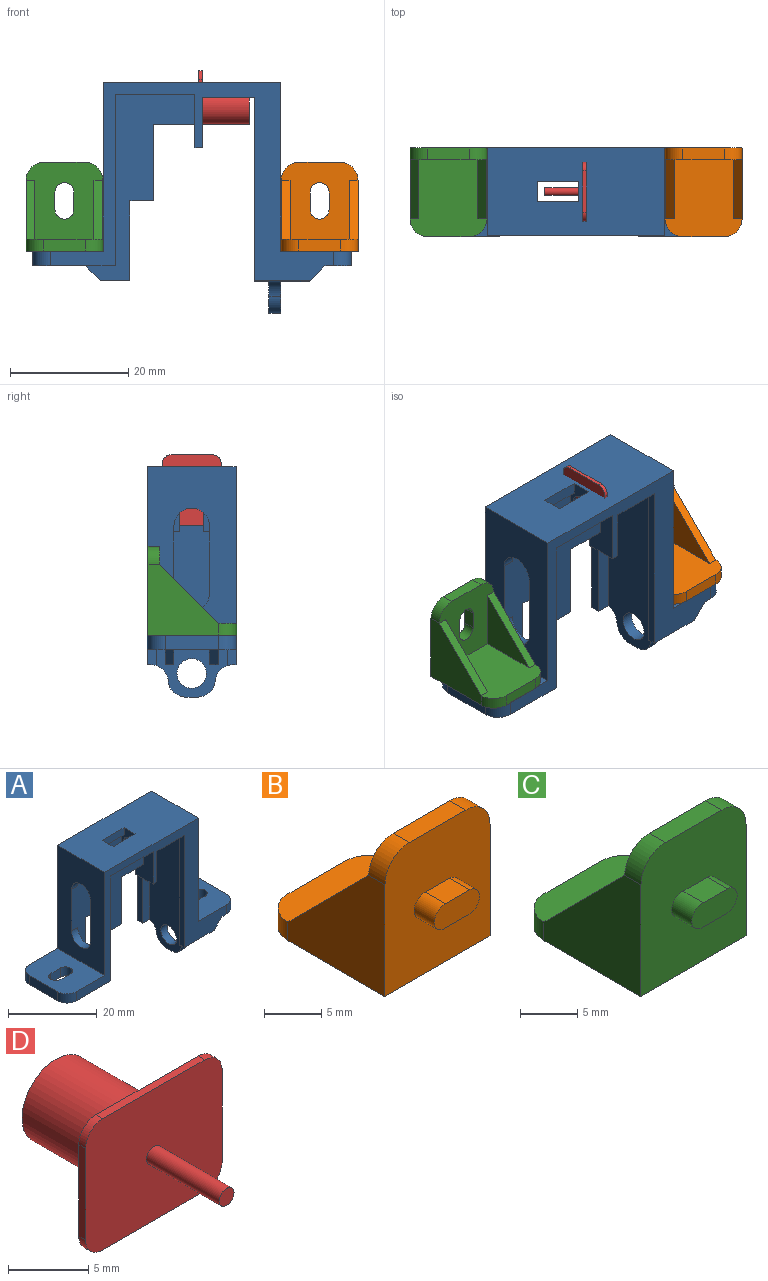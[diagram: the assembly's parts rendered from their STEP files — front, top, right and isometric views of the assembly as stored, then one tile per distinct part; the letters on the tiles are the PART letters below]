
ASSEMBLY  parts=4 mates=3
PART A: 82 faces, bbox 54x15x39 mm
  f0: plane 31.5x18.5mm, normal (0,1,0), area 195.1mm2, adj f3,f13,f16,f20,f22,f38,f54,f73
  f1: plane 31.5x18.5mm, normal (0,-1,0), area 195.1mm2, adj f2,f12,f16,f19,f22,f39,f54,f74
  f2: plane 5x1.5mm, normal (0,0,-1), area 7.5mm2, adj f1,f36,f74,f78
  f3: plane 5x1.5mm, normal (0,0,-1), area 7.5mm2, adj f0,f37,f73,f75
  f4: plane 15x12mm, normal (0,0,-1), area 136mm2, adj f7,f21,f25,f32,f33,f34,f35,f45
  f5: plane 11.25x4.9mm, normal (0,0,-1), area 51.4mm2, adj f6,f7,f43,f57,f61,f62
  f6: plane 38x12mm, normal (-1,0,0), area 401.7mm2, adj f5,f57,f58,f60,f61,f68,f69,f70
  f7: plane 48x33.5mm, normal (0,1,0), area 336mm2, adj f4,f5,f10,f13,f16,f18,f22,f23
  f8: plane 3x3mm, normal (1,0,0), area 1.9mm2, adj f36,f54,f56
  f9: plane 3x3mm, normal (1,0,0), area 1.9mm2, adj f37,f54,f56
  f10: plane 28.5x15mm, normal (-1,0,0), area 330.2mm2, adj f7,f18,f21,f24,f36,f37,f55,f56
  f11: plane 7x0.75mm, normal (0,0,-1), area 5.3mm2, adj f16,f40,f41,f53
  f12: plane 13.5x3mm, normal (0,0,-1), area 40.5mm2, adj f1,f16,f21,f39
  f13: plane 13.5x3mm, normal (0,0,-1), area 40.5mm2, adj f0,f7,f16,f38
  f14: plane 9.5x6mm, normal (1,0,0), area 42.9mm2, adj f22,f36,f37,f55
  f15: plane 5.5x1.25mm, normal (0,0,-1), area 6.9mm2, adj f16,f21,f43,f51
  f16: plane 15x11mm, normal (-1,0,0), area 87.7mm2, adj f0,f1,f7,f11,f12,f13,f15,f17
  f17: plane 7x0.75mm, normal (0,0,-1), area 5.2mm2, adj f16,f41,f42,f52
  f18: plane 30x15mm, normal (0,0,1), area 425.5mm2, adj f7,f10,f16,f21,f26,f40,f41,f42
  f19: plane 13x1.5mm, normal (1,0,0), area 19.5mm2, adj f1,f36,f54,f77
  f20: plane 13x1.5mm, normal (1,0,0), area 19.5mm2, adj f0,f37,f54,f76
  f21: plane 48x33.5mm, normal (0,-1,0), area 336mm2, adj f4,f10,f12,f15,f16,f18,f22,f23
  f22: plane 15x14mm, normal (0,0,-1), area 173.5mm2, adj f0,f1,f7,f14,f21,f27,f28,f29
  f23: plane 15x12mm, normal (0,0,1), area 158.5mm2, adj f7,f21,f25,f26,f32,f33,f34,f35
  f24: plane 15x12mm, normal (0,0,1), area 158.5mm2, adj f7,f10,f21,f27,f28,f29,f30,f31
  f25: plane 9x2.5mm, normal (1,0,0), area 22.5mm2, adj f4,f23,f45,f47
  f26: plane 28.5x15mm, normal (1,0,0), area 427.5mm2, adj f7,f18,f21,f23
  f27: plane 9x2.5mm, normal (-1,0,0), area 22.5mm2, adj f22,f24,f46,f48
  f28: plane 3x2.5mm, normal (0,1,0), area 7.5mm2, adj f22,f24,f29,f31
  f29: cylinder r=1.6mm len=3.2mm, axis (0,0,-1), area 12.6mm2, adj f22,f24,f28,f30
  f30: plane 3x2.5mm, normal (0,-1,0), area 7.5mm2, adj f22,f24,f29,f31
  f31: cylinder r=1.6mm len=3.2mm, axis (0,0,-1), area 12.6mm2, adj f22,f24,f28,f30
  f32: cylinder r=1.6mm len=3.2mm, axis (0,0,-1), area 12.6mm2, adj f4,f23,f33,f35
  f33: plane 3x2.5mm, normal (0,-1,0), area 7.5mm2, adj f4,f23,f32,f34
  f34: cylinder r=1.6mm len=3.2mm, axis (0,0,-1), area 12.6mm2, adj f4,f23,f33,f35
  f35: plane 3x2.5mm, normal (0,1,0), area 7.5mm2, adj f4,f23,f32,f34
  f36: plane 26.5x11.5mm, normal (0,1,0), area 150.6mm2, adj f2,f8,f10,f14,f19,f22,f54,f55
  f37: plane 26.5x11.5mm, normal (0,-1,0), area 150.6mm2, adj f3,f9,f10,f14,f20,f22,f54,f55
  f38: plane 29x3mm, normal (1,0,0), area 87mm2, adj f0,f7,f13,f22
  f39: plane 29x3mm, normal (1,0,0), area 87mm2, adj f1,f12,f21,f22
  f40: plane 7x2mm, normal (0,1,0), area 14mm2, adj f11,f16,f18,f41
  f41: plane 7x5mm, normal (1,0,0), area 32mm2, adj f11,f17,f18,f40,f42,f52,f53,f54
  f42: plane 7x2mm, normal (0,-1,0), area 14mm2, adj f16,f17,f18,f41
  f43: plane 15x10mm, normal (1,0,0), area 98.7mm2, adj f5,f7,f15,f21,f44,f49,f50,f51
  f44: plane 5.5x1.25mm, normal (0,0,-1), area 6.9mm2, adj f7,f16,f43,f49
  f45: cylinder r=3mm len=3mm, axis (0,0,1), area 11.8mm2, adj f4,f7,f23,f25
  f46: cylinder r=3mm len=3mm, axis (0,0,-1), area 11.8mm2, adj f7,f22,f24,f27
  f47: cylinder r=3mm len=3mm, axis (0,0,-1), area 11.8mm2, adj f4,f21,f23,f25
  f48: cylinder r=3mm len=3mm, axis (0,0,1), area 11.8mm2, adj f21,f22,f24,f27
  f49: plane 7x1.25mm, normal (0,-1,0), area 8.8mm2, adj f16,f43,f44,f50
  f50: cylinder r=2mm len=4mm, axis (1,0,0), area 7.9mm2, adj f16,f43,f49,f51
  f51: plane 7x1.25mm, normal (0,1,0), area 8.8mm2, adj f15,f16,f43,f50
  f52: plane 7x5mm, normal (0,-1,0), area 35mm2, adj f16,f17,f41,f54
  f53: plane 7x5mm, normal (0,1,0), area 35mm2, adj f11,f16,f41,f54
  f54: plane 13.5x9mm, normal (0,0,-1), area 67mm2, adj f0,f1,f8,f9,f16,f19,f20,f36
  f55: cylinder r=3mm len=6mm, axis (-1,0,0), area 18.8mm2, adj f10,f14,f36,f37
  f56: cylinder r=3mm len=6mm, axis (-1,0,0), area 18.8mm2, adj f8,f9,f10,f36,f37
  f57: cylinder r=3mm len=11.25mm, axis (1,0,0), area 70.7mm2, adj f5,f6,f43,f58
  f58: plane 11.25x4.9mm, normal (0,0,-1), area 51.4mm2, adj f6,f21,f43,f57,f59,f60
  f59: plane 31.16x1.5mm, normal (-1,0,0), area 46.6mm2, adj f21,f58,f60,f65,f80
  f60: plane 31.16x2.5mm, normal (0,1,0), area 77.9mm2, adj f6,f58,f59,f80
  f61: plane 31.16x2.5mm, normal (0,-1,0), area 77.9mm2, adj f5,f6,f62,f81
  f62: plane 31.16x1.5mm, normal (-1,0,0), area 46.6mm2, adj f5,f7,f61,f67,f81
  f63: plane 12x8mm, normal (1,0,0), area 54.1mm2, adj f4,f64,f66,f68,f69,f70,f79,f80
  f64: plane 7.5x2.66mm, normal (0,1,0), area 16.4mm2, adj f4,f63,f71,f80
  f65: plane 9.5x0.52mm, normal (0,0,-1), area 4.9mm2, adj f21,f59,f71,f80
  f66: plane 7.5x2.66mm, normal (0,-1,0), area 16.4mm2, adj f4,f63,f72,f81
  f67: plane 9.5x0.52mm, normal (0,0,-1), area 4.9mm2, adj f7,f62,f72,f81
  f68: plane 2x2mm, normal (0,0,-1), area 4mm2, adj f6,f63,f69,f70
  f69: cylinder r=3mm len=2.99mm, axis (-1,0,0), area 8.9mm2, adj f6,f63,f68,f81
  f70: cylinder r=3mm len=2.99mm, axis (1,0,0), area 8.9mm2, adj f6,f63,f68,f80
  f71: plane 2.66x2.66mm, normal (0.71,0,-0.71), area 5.4mm2, adj f4,f21,f64,f65,f80
  f72: plane 2.66x2.66mm, normal (0.71,0,-0.71), area 5.4mm2, adj f4,f7,f66,f67,f81
  f73: plane 2.5x2.5mm, normal (-0.71,0,-0.71), area 5.3mm2, adj f0,f3,f22,f37
  f74: plane 2.5x2.5mm, normal (-0.71,0,-0.71), area 5.3mm2, adj f1,f2,f22,f36
  f75: plane 13.5x1.5mm, normal (1,0,0), area 20.2mm2, adj f0,f3,f37,f76
  f76: plane 4x1.5mm, normal (0,0,-1), area 6mm2, adj f0,f20,f37,f75
  f77: plane 4x1.5mm, normal (0,0,-1), area 6mm2, adj f1,f19,f36,f78
  f78: plane 13.5x1.5mm, normal (1,0,0), area 20.3mm2, adj f1,f2,f36,f77
  f79: cylinder r=2.5mm len=5mm, axis (1,0,0), area 31.4mm2, adj f6,f63
  f80: cylinder r=3mm len=9.5mm, axis (1,0,0), area 16.3mm2, adj f6,f59,f60,f63,f64,f65,f70,f71
  f81: cylinder r=3mm len=9.5mm, axis (-1,0,0), area 16.3mm2, adj f6,f61,f62,f63,f66,f67,f69,f72
PART B: 25 faces, bbox 13x17.5x15 mm
  f0: plane 13x13mm, normal (0,0,1), area 117.5mm2, adj f1,f6,f7,f8,f9,f10,f19,f20
  f1: plane 13x13mm, normal (0,1,0), area 135.1mm2, adj f0,f11,f17,f18,f21,f22,f23,f24
  f2: plane 15x13mm, normal (0,-1,0), area 178mm2, adj f3,f4,f5,f11,f12,f13,f14,f15
  f3: plane 15x13mm, normal (0,0,-1), area 173.5mm2, adj f2,f4,f5,f6,f7,f8,f9,f10
  f4: plane 12x12mm, normal (1,0,0), area 94mm2, adj f2,f3,f17,f20,f23
  f5: plane 12x12mm, normal (-1,0,0), area 94mm2, adj f2,f3,f18,f19,f24
  f6: plane 7x2mm, normal (0,1,0), area 14mm2, adj f0,f3,f19,f20
  f7: cylinder r=1.6mm len=3.2mm, axis (0,0,-1), area 10.1mm2, adj f0,f3,f8,f10
  f8: plane 3x2mm, normal (-1,0,0), area 6mm2, adj f0,f3,f7,f9
  f9: cylinder r=1.6mm len=3.2mm, axis (0,0,-1), area 10.1mm2, adj f0,f3,f8,f10
  f10: plane 3x2mm, normal (1,0,0), area 6mm2, adj f0,f3,f7,f9
  f11: plane 7x2mm, normal (0,0,1), area 14mm2, adj f1,f2,f17,f18
  f12: cylinder r=1.3mm len=2.6mm, axis (0,1,0), area 10.5mm2, adj f2,f13,f15,f16
  f13: plane 3x2.5mm, normal (0,0,-1), area 7.5mm2, adj f2,f12,f14,f16
  f14: cylinder r=1.3mm len=2.6mm, axis (0,1,0), area 10mm2, adj f2,f13,f15,f16
  f15: plane 3x2.5mm, normal (0,0,1), area 7.5mm2, adj f2,f12,f14,f16
  f16: plane 5.6x2.6mm, normal (0,-1,0), area 13.1mm2, adj f12,f13,f14,f15
  f17: cylinder r=3mm len=3mm, axis (0,1,0), area 9.4mm2, adj f1,f2,f4,f11
  f18: cylinder r=3mm len=3mm, axis (0,1,0), area 9.4mm2, adj f1,f2,f5,f11
  f19: cylinder r=3mm len=3mm, axis (0,0,1), area 9.4mm2, adj f0,f3,f5,f6
  f20: cylinder r=3mm len=3mm, axis (0,0,-1), area 9.4mm2, adj f0,f3,f4,f6
  f21: plane 10x10mm, normal (1,0,0), area 50mm2, adj f0,f1,f24
  f22: plane 10x10mm, normal (-1,0,0), area 50mm2, adj f0,f1,f23
  f23: plane 10x10mm, normal (0,0.71,0.71), area 21.2mm2, adj f0,f1,f4,f22
  f24: plane 10x10mm, normal (0,0.71,0.71), area 21.2mm2, adj f0,f1,f5,f21
PART C: 25 faces, bbox 13x17.5x15 mm
  f0: plane 13x13mm, normal (0,0,1), area 117.5mm2, adj f1,f6,f7,f8,f9,f10,f19,f20
  f1: plane 13x13mm, normal (0,1,0), area 135.1mm2, adj f0,f11,f17,f18,f21,f22,f23,f24
  f2: plane 15x13mm, normal (0,-1,0), area 178mm2, adj f3,f4,f5,f11,f12,f13,f14,f15
  f3: plane 15x13mm, normal (0,0,-1), area 173.5mm2, adj f2,f4,f5,f6,f7,f8,f9,f10
  f4: plane 12x12mm, normal (1,0,0), area 94mm2, adj f2,f3,f17,f20,f23
  f5: plane 12x12mm, normal (-1,0,0), area 94mm2, adj f2,f3,f18,f19,f24
  f6: plane 7x2mm, normal (0,1,0), area 14mm2, adj f0,f3,f19,f20
  f7: cylinder r=1.6mm len=3.2mm, axis (0,0,-1), area 10.1mm2, adj f0,f3,f8,f10
  f8: plane 3x2mm, normal (-1,0,0), area 6mm2, adj f0,f3,f7,f9
  f9: cylinder r=1.6mm len=3.2mm, axis (0,0,-1), area 10.1mm2, adj f0,f3,f8,f10
  f10: plane 3x2mm, normal (1,0,0), area 6mm2, adj f0,f3,f7,f9
  f11: plane 7x2mm, normal (0,0,1), area 14mm2, adj f1,f2,f17,f18
  f12: cylinder r=1.3mm len=2.6mm, axis (0,1,0), area 10.5mm2, adj f2,f13,f15,f16
  f13: plane 3x2.5mm, normal (0,0,-1), area 7.5mm2, adj f2,f12,f14,f16
  f14: cylinder r=1.3mm len=2.6mm, axis (0,1,0), area 10mm2, adj f2,f13,f15,f16
  f15: plane 3x2.5mm, normal (0,0,1), area 7.5mm2, adj f2,f12,f14,f16
  f16: plane 5.6x2.6mm, normal (0,-1,0), area 13.1mm2, adj f12,f13,f14,f15
  f17: cylinder r=3mm len=3mm, axis (0,1,0), area 9.4mm2, adj f1,f2,f4,f11
  f18: cylinder r=3mm len=3mm, axis (0,1,0), area 9.4mm2, adj f1,f2,f5,f11
  f19: cylinder r=3mm len=3mm, axis (0,0,1), area 9.4mm2, adj f0,f3,f5,f6
  f20: cylinder r=3mm len=3mm, axis (0,0,-1), area 9.4mm2, adj f0,f3,f4,f6
  f21: plane 10x10mm, normal (1,0,0), area 50mm2, adj f0,f1,f24
  f22: plane 10x10mm, normal (-1,0,0), area 50mm2, adj f0,f1,f23
  f23: plane 10x10mm, normal (0,0.71,0.71), area 21.2mm2, adj f0,f1,f4,f22
  f24: plane 10x10mm, normal (0,0.71,0.71), area 21.2mm2, adj f0,f1,f5,f21
PART D: 14 faces, bbox 12x15x10 mm
  f0: cylinder r=3mm len=8mm, axis (0,-1,0), area 150.8mm2, adj f1,f2
  f1: plane 6x6mm, normal (0,1,0), area 28.3mm2, adj f0
  f2: plane 12x10mm, normal (0,1,0), area 89.8mm2, adj f0,f3,f4,f5,f6,f7,f8,f9
  f3: plane 7x0.6mm, normal (1,0,0), area 4.2mm2, adj f2,f4,f10,f11
  f4: cylinder r=1.5mm len=1.5mm, axis (0,1,0), area 1.4mm2, adj f2,f3,f5,f11
  f5: plane 9x0.6mm, normal (0,0,1), area 5.4mm2, adj f2,f4,f6,f11
  f6: cylinder r=1.5mm len=1.5mm, axis (0,1,0), area 1.4mm2, adj f2,f5,f7,f11
  f7: plane 7x0.6mm, normal (-1,0,0), area 4.2mm2, adj f2,f6,f8,f11
  f8: cylinder r=1.5mm len=1.5mm, axis (0,1,0), area 1.4mm2, adj f2,f7,f9,f11
  f9: plane 9x0.6mm, normal (0,0,-1), area 5.4mm2, adj f2,f8,f10,f11
  f10: cylinder r=1.5mm len=1.5mm, axis (0,1,0), area 1.4mm2, adj f2,f3,f9,f11
  f11: plane 12x10mm, normal (0,-1,0), area 116.7mm2, adj f3,f4,f5,f6,f7,f8,f9,f10
  f12: cylinder r=0.65mm len=6.4mm, axis (0,1,0), area 26.1mm2, adj f11,f13
  f13: plane 1.3x1.3mm, normal (0,-1,0), area 1.3mm2, adj f12
PLACE A t=(-10.54,17.36,-12.65)mm fixed
PLACE B rot(axis=(1,0,0),90deg) t=(19.56,17.27,-12.65)mm
PLACE C rot(axis=(1,0,0),90deg) t=(-23.64,17.27,-12.65)mm
PLACE D rot(axis=(0.58,0.58,-0.58),120deg) t=(6.18,9.86,11.85)mm
MATE fastened C.f16 <-> A.f22  axis (0,0,-1) through (-17.04,9.86,-15.15)mm
MATE fastened D.f12 <-> A.f50  axis (-1,0,0) through (5.58,9.86,11.85)mm
MATE fastened B.f16 <-> A.f4  axis (0,0,-1) through (25.96,9.86,-15.15)mm
